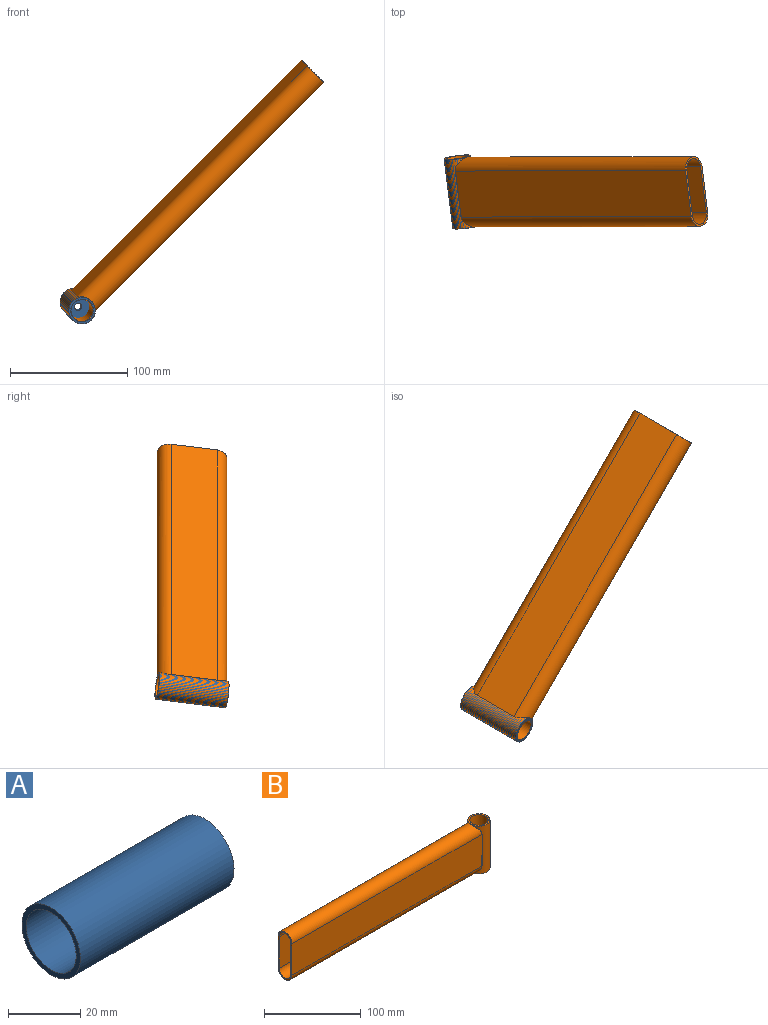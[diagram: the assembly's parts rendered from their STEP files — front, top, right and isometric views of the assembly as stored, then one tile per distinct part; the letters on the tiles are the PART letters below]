
ASSEMBLY  parts=2 mates=1
PART A: 8 faces, bbox 60.2x22.9x22.9 mm
  f0: cylinder r=3.17mm len=6.86mm, axis (-1,0,0), area 136.8mm2, adj f1,f2
  f1: plane 19.56x19.56mm, normal (1,0,0), area 268.8mm2, adj f0,f4
  f2: plane 19.56x19.56mm, normal (-1,0,0), area 268.8mm2, adj f0,f3
  f3: cylinder r=9.78mm len=26.67mm, axis (-1,0,0), area 1638.7mm2, adj f2,f7
  f4: cylinder r=9.78mm len=26.67mm, axis (-1,0,0), area 1638.7mm2, adj f1,f6
  f5: cylinder r=11.43mm len=60.2mm, axis (-1,0,0), area 4323.2mm2, adj f6,f7
  f6: plane 22.86x22.86mm, normal (1,0,0), area 110mm2, adj f4,f5
  f7: plane 22.86x22.86mm, normal (-1,0,0), area 110mm2, adj f3,f5
PART B: 16 faces, bbox 294.9x22.9x60.2 mm
  f0: cylinder r=10.16mm len=277.8mm, axis (-1,0,0), area 8771.3mm2, adj f6,f7,f8,f9,f10,f13
  f1: cylinder r=8.38mm len=275.69mm, axis (-1,0,0), area 7209.3mm2, adj f2,f4,f10,f15
  f2: plane 275.69x39.88mm, normal (0,1,0), area 10994.1mm2, adj f1,f3,f10,f15
  f3: cylinder r=8.38mm len=275.69mm, axis (-1,0,0), area 7209.3mm2, adj f2,f4,f10,f15
  f4: plane 275.69x39.88mm, normal (0,-1,0), area 10994.1mm2, adj f1,f3,f10,f15
  f5: cylinder r=10.16mm len=277.8mm, axis (-1,0,0), area 8771.3mm2, adj f6,f7,f8,f9,f10,f13
  f6: plane 44.19x0.23mm, normal (1,0,0), area 9.9mm2, adj f0,f5,f8,f13
  f7: plane 44.19x0.23mm, normal (1,0,0), area 9.9mm2, adj f0,f5,f9,f13
  f8: plane 277.8x39.88mm, normal (0,1,0), area 11078.1mm2, adj f0,f5,f6,f10
  f9: plane 277.8x39.88mm, normal (0,-1,0), area 11078.1mm2, adj f0,f5,f7,f10
  f10: plane 60.2x20.32mm, normal (-1,0,0), area 245.4mm2, adj f0,f1,f2,f3,f4,f5,f8,f9
  f11: plane 22.86x22.86mm, normal (0,0,-1), area 133mm2, adj f13,f14
  f12: plane 22.86x22.86mm, normal (0,0,1), area 133mm2, adj f13,f14
  f13: cylinder r=11.43mm len=60.2mm, axis (0,0,-1), area 2992.4mm2, adj f0,f5,f6,f7,f11,f12
  f14: cylinder r=9.4mm len=60.2mm, axis (0,0,1), area 3554.7mm2, adj f11,f12
  f15: cylinder r=11.43mm len=56.64mm, axis (0,0,-1), area 990.3mm2, adj f1,f2,f3,f4
PLACE A rot(axis=(-0.71,0.66,-0.22),141.9deg) t=(154.91,-4.27,-3.83)mm
PLACE B rot(axis=(0.26,0.74,-0.62),145.9deg) t=(355.35,-4.27,196.61)mm
MATE fastened A.f5 <-> B.f13  axis (-0.12,0.98,0.12) through (151.21,25.37,-0.13)mm
